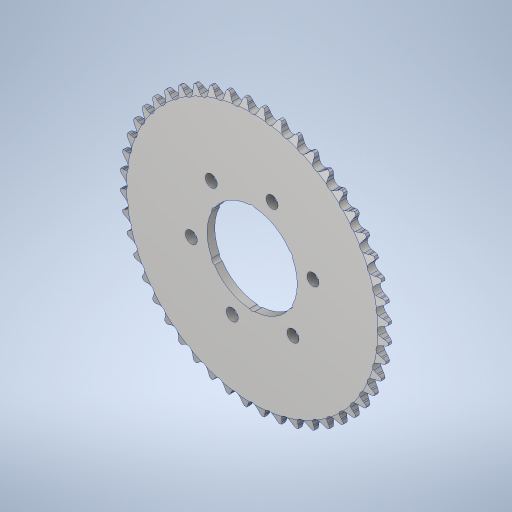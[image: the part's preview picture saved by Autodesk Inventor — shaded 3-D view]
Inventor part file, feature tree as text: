
AUTODESK INVENTOR PART (.ipt)
format: ipt  version: 2023.3 (Build 273359000, 359)  size: 1,260,544 bytes
history: native  units: in
note: dims shown in document units (in); Inventor stores cm internally (conversion verified against a paired STEP export)
features: sketch x2, other x2, extrude x1, hole x1, pattern_circular x1, plane x1, boolean_combine x1
ambient origin geometry x8: Origin, YZ Plane, XZ Plane, XY Plane, X Axis, Y Axis, Z Axis, Center Point
bodies: Solid1 (feature_tree)
feature tree (9):
  extrude  "Extrusion1"  TaperAngle=0.0deg  [1 undecoded]
  hole  "Hole2"  [1 undecoded]
  pattern_circular  "Circular Pattern1"  [2 undecoded]
  plane  "Work Plane1"
  sketch  "Sketch1"  dims[d0=2.0in d1=0.0in d2=0.0in]
  sketch  "Sketch2"  dims[d3=2.75in d15=0.266in d16=0.75in d17=0.375in d18=0.25in d19=0.5635in d20=1.0in d21=0.8108in d22=2.3622in d23=2.4737in]
  other  "Work Axis1"
  other  "Work Axis2"
  boolean_combine  "Combine1"
note: 4 required parameter values undecoded (feature->parameter linkage not recoverable at this tier; creation-order binding heuristic only, values carry confidence <= 0.55)
